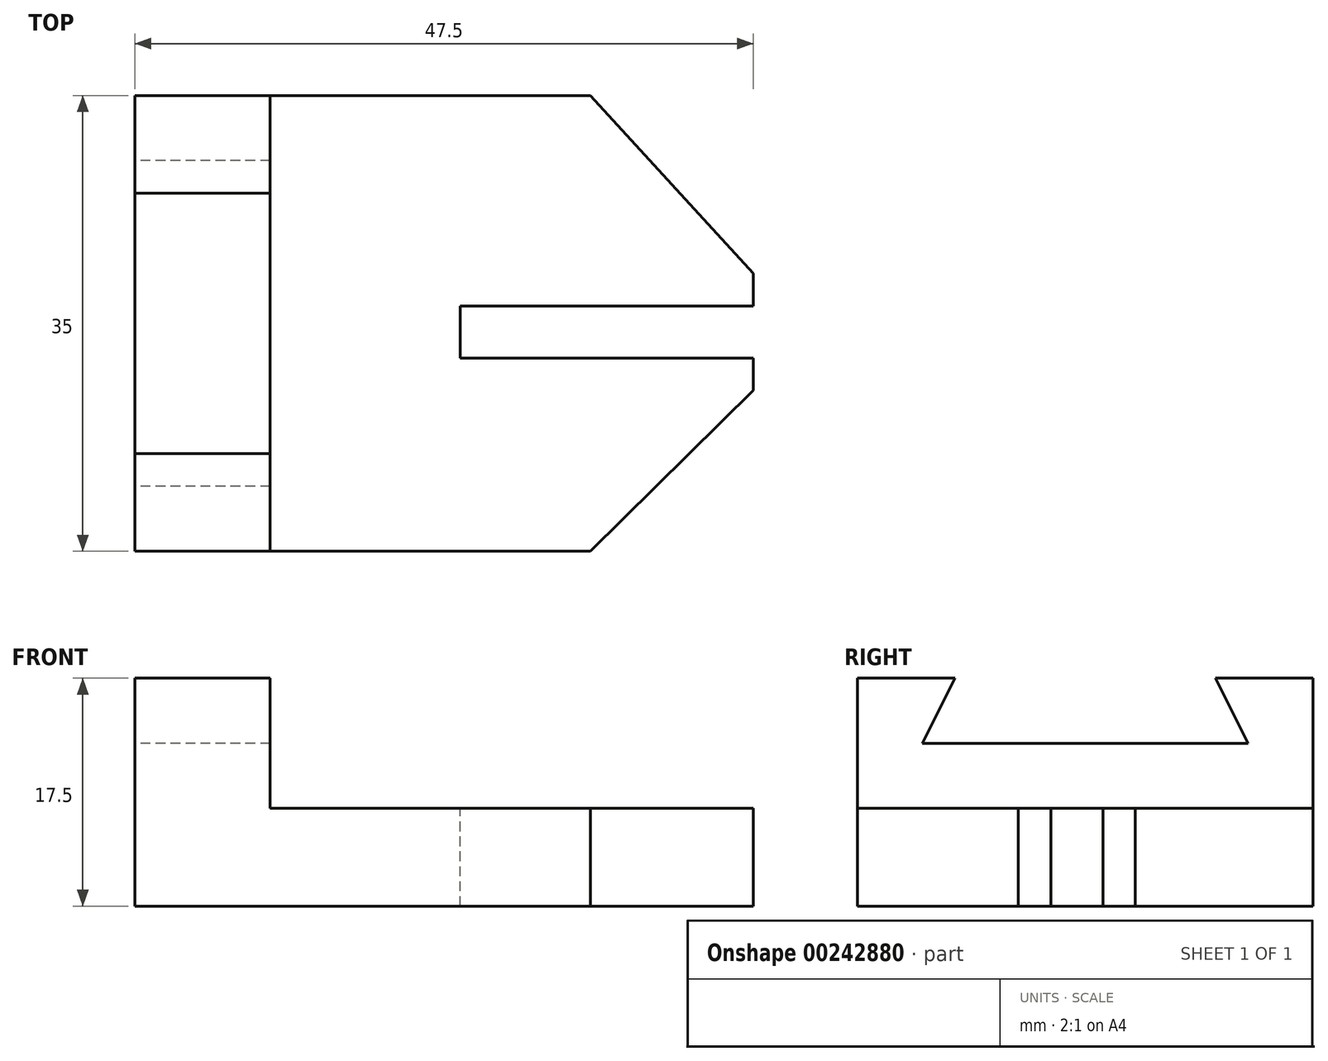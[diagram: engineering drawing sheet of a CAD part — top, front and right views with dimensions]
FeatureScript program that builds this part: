
annotation { "Feature Type Name" : "Feature", "Feature Type Description" : "" }
export const myFeature = defineFeature(function(context is Context, id is Id, definition is map)
    precondition{}
    {
        {
            var Q0;
            Q0=qCreatedBy(makeId("Top.planeOp"),FACE);
            var sketch = newSketch(context, id + "F0", { "sketchPlane" : qUnion([Q0])});
            skLineSegment(sketch, "E0.bottom", {"start": v(-29.86, 27.4) * mm, "end": v(17.64, 27.4) * mm});
            skLineSegment(sketch, "E0.top", {"start": v(-29.86, -7.6) * mm, "end": v(17.64, -7.6) * mm});
            skLineSegment(sketch, "E0.left", {"start": v(-29.86, 27.4) * mm, "end": v(-29.86, -7.6) * mm});
            skLineSegment(sketch, "E0.right", {"start": v(17.64, 27.4) * mm, "end": v(17.64, -7.6) * mm});
            skSolve(sketch);
        }
        {
            var Q0;
            Q0=makeQuery(id+"F0.imprint","IMPRINT",FACE,{"disambiguationData":[TD([[makeQuery(id+"F0.imprint","IMPRINT",EDGE,{"derivedFrom":sQuery(id+"F0.wireOp",EDGE,"E0.bottom")}),-1.0]])]});
            extrude(context, id + "F1", {"entities" : qUnion([Q0]), "depth" : 17.5 * mm});
        }
        {
            var Q0;
            Q0=makeQuery(id+"F1.opExtrude","SWEPT_FACE",FACE,{"disambiguationData":[OSD([sQuery(id+"F0.wireOp",EDGE,"E0.top")])]});
            var sketch = newSketch(context, id + "F2", { "sketchPlane" : qUnion([Q0])});
            skLineSegment(sketch, "E1", {"start": v(17.64, 0) * mm, "end": v(17.64, 7.5) * mm});
            skLineSegment(sketch, "E2", {"start": v(-29.86, 17.5) * mm, "end": v(-29.86, 7.5) * mm});
            skLineSegment(sketch, "E3", {"start": v(-29.86, 7.5) * mm, "end": v(17.64, 7.5) * mm});
            skLineSegment(sketch, "E4", {"start": v(-19.46, 17.5) * mm, "end": v(-19.46, 7.5) * mm});
            skSolve(sketch);
        }
        {
            var Q0;
            {var subQ4=sQuery(id+"F2.wireOp",EDGE,"E4");Q0=makeQuery(id+"F2.imprint","IMPRINT",FACE,{"disambiguationData":[TD([[makeQuery(id+"F2.imprint","IMPRINT",EDGE,{"derivedFrom":subQ4}),1.0]])]});}
            extrude(context, id + "F3", {"entities" : qUnion([Q0]), "operationType" : NewBodyOperationType.REMOVE, "endBound" : BoundingType.THROUGH_ALL, "oppositeDirection" : true, "depth" : 25 * mm});
        }
        {
            var Q0;
            Q0=makeQuery(id+"F1.opExtrude","SWEPT_FACE",FACE,{"disambiguationData":[OSD([sQuery(id+"F0.wireOp",EDGE,"E0.left")])]});
            var sketch = newSketch(context, id + "F4", { "sketchPlane" : qUnion([Q0])});
            skLineSegment(sketch, "E5", {"start": v(-27.4, 12.5) * mm, "end": v(-22.4, 12.5) * mm});
            skLineSegment(sketch, "E6", {"start": v(7.6, 12.5) * mm, "end": v(2.6, 12.5) * mm});
            skLineSegment(sketch, "E7", {"start": v(7.6, 17.5) * mm, "end": v(0.1, 17.5) * mm});
            skLineSegment(sketch, "E8", {"start": v(-27.4, 17.5) * mm, "end": v(-19.9, 17.5) * mm});
            skLineSegment(sketch, "E9", {"start": v(-22.4, 12.5) * mm, "end": v(-19.9, 17.5) * mm});
            skLineSegment(sketch, "E10", {"start": v(-22.4, 12.5) * mm, "end": v(2.6, 12.5) * mm});
            skLineSegment(sketch, "E11", {"start": v(2.6, 12.5) * mm, "end": v(0.1, 17.5) * mm});
            skSolve(sketch);
        }
        {
            var Q0;
            {var subQ0=sQuery(id+"F4.wireOp",EDGE,"E9");Q0=makeQuery(id+"F4.imprint","IMPRINT",FACE,{"disambiguationData":[TD([[makeQuery(id+"F4.imprint","IMPRINT",EDGE,{"derivedFrom":subQ0}),-1.0]])]});}
            extrude(context, id + "F5", {"entities" : qUnion([Q0]), "operationType" : NewBodyOperationType.REMOVE, "endBound" : BoundingType.THROUGH_ALL, "oppositeDirection" : true, "depth" : 25 * mm});
        }
        {
            var Q0;
            Q0=makeQuery(id+"F3.boolean.opBoolean","COPY",FACE,{"derivedFrom":makeQuery(id+"F3.opExtrude","SWEPT_FACE",FACE,{"disambiguationData":[OSD([sQuery(id+"F2.wireOp",EDGE,"E3")])]})});
            var sketch = newSketch(context, id + "F6", { "sketchPlane" : qUnion([Q0])});
            skLineSegment(sketch, "E12", {"start": v(17.64, -7.6) * mm, "end": v(5.14, -7.6) * mm});
            skLineSegment(sketch, "E13", {"start": v(17.64, 27.4) * mm, "end": v(5.14, 27.4) * mm});
            skLineSegment(sketch, "E14", {"start": v(17.64, 7.25) * mm, "end": v(-4.86, 7.25) * mm});
            skLineSegment(sketch, "E15", {"start": v(-4.86, 7.25) * mm, "end": v(-4.86, 11.25) * mm});
            skLineSegment(sketch, "E16", {"start": v(-4.86, 11.25) * mm, "end": v(17.64, 11.25) * mm});
            skLineSegment(sketch, "E17", {"start": v(17.64, 11.25) * mm, "end": v(17.64, 13.75) * mm});
            skLineSegment(sketch, "E18", {"start": v(17.64, 7.25) * mm, "end": v(17.64, 4.75) * mm});
            skLineSegment(sketch, "E19", {"start": v(5.14, -7.6) * mm, "end": v(17.64, 4.75) * mm});
            skLineSegment(sketch, "E20", {"start": v(17.64, 13.75) * mm, "end": v(5.14, 27.4) * mm});
            skSolve(sketch);
        }
        {
            var Q0;
            {var subQ0=sQuery(id+"F6.wireOp",EDGE,"E12");Q0=makeQuery(id+"F6.imprint","IMPRINT",FACE,{"disambiguationData":[TD([[makeQuery(id+"F6.imprint","IMPRINT",EDGE,{"derivedFrom":subQ0}),1.0]])]});}
            var Q1;
            {var subQ0=sQuery(id+"F6.wireOp",EDGE,"E13");Q1=makeQuery(id+"F6.imprint","IMPRINT",FACE,{"disambiguationData":[TD([[makeQuery(id+"F6.imprint","IMPRINT",EDGE,{"derivedFrom":subQ0}),1.0]])]});}
            var Q2;
            {var subQ0=sQuery(id+"F6.wireOp",EDGE,"E14");Q2=makeQuery(id+"F6.imprint","IMPRINT",FACE,{"disambiguationData":[TD([[makeQuery(id+"F6.imprint","IMPRINT",EDGE,{"derivedFrom":subQ0}),-1.0]])]});}
            extrude(context, id + "F7", {"entities" : qUnion([Q0, Q1, Q2]), "operationType" : NewBodyOperationType.REMOVE, "endBound" : BoundingType.THROUGH_ALL, "oppositeDirection" : true, "depth" : 25 * mm});
        }
    });
